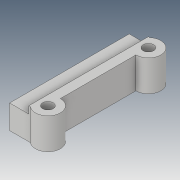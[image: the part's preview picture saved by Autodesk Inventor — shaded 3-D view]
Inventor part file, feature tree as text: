
AUTODESK INVENTOR PART (.ipt)
format: ipt  version: 2019 (Build 230136000, 136)  size: 122,880 bytes
history: native  units: mm
features: extrude x4, sketch x3, projected_geometry x1
ambient origin geometry x8: Origin, YZ Plane, XZ Plane, XY Plane, X Axis, Y Axis, Z Axis, Center Point
bodies: Solid1 (feature_tree)
feature tree (8):
  extrude  "Extrusion1"  Depth=6.0mm
  sketch  "Sketch2"  dims[d2=4.5mm d3=0.0mm d4=2.0mm]
  extrude  "Extrusion3"  Depth=2.0mm
  extrude  "Extrusion4"  TaperAngle=0.0deg  [1 undecoded]
  extrude  "Extrusion5"  Depth=2.0mm
  sketch  "Sketch1"  dims[d0=25.0mm d1=6.0mm]
  sketch  "Sketch3"  dims[d5=2.2mm d6=0.0mm d8=2.0mm d9=2.2mm d10=0.0mm d11=2.0mm d17=1.5mm d18=1.5mm d19=2.0mm d20=4.5mm d21=0.0mm d22=0.0mm d23=2.0mm d24=0.0mm d25=0.5mm d26=0.0mm]
  projected_geometry  "Projected Loop1"
note: 1 required parameter value undecoded (feature->parameter linkage not recoverable at this tier; creation-order binding heuristic only, values carry confidence <= 0.55)
